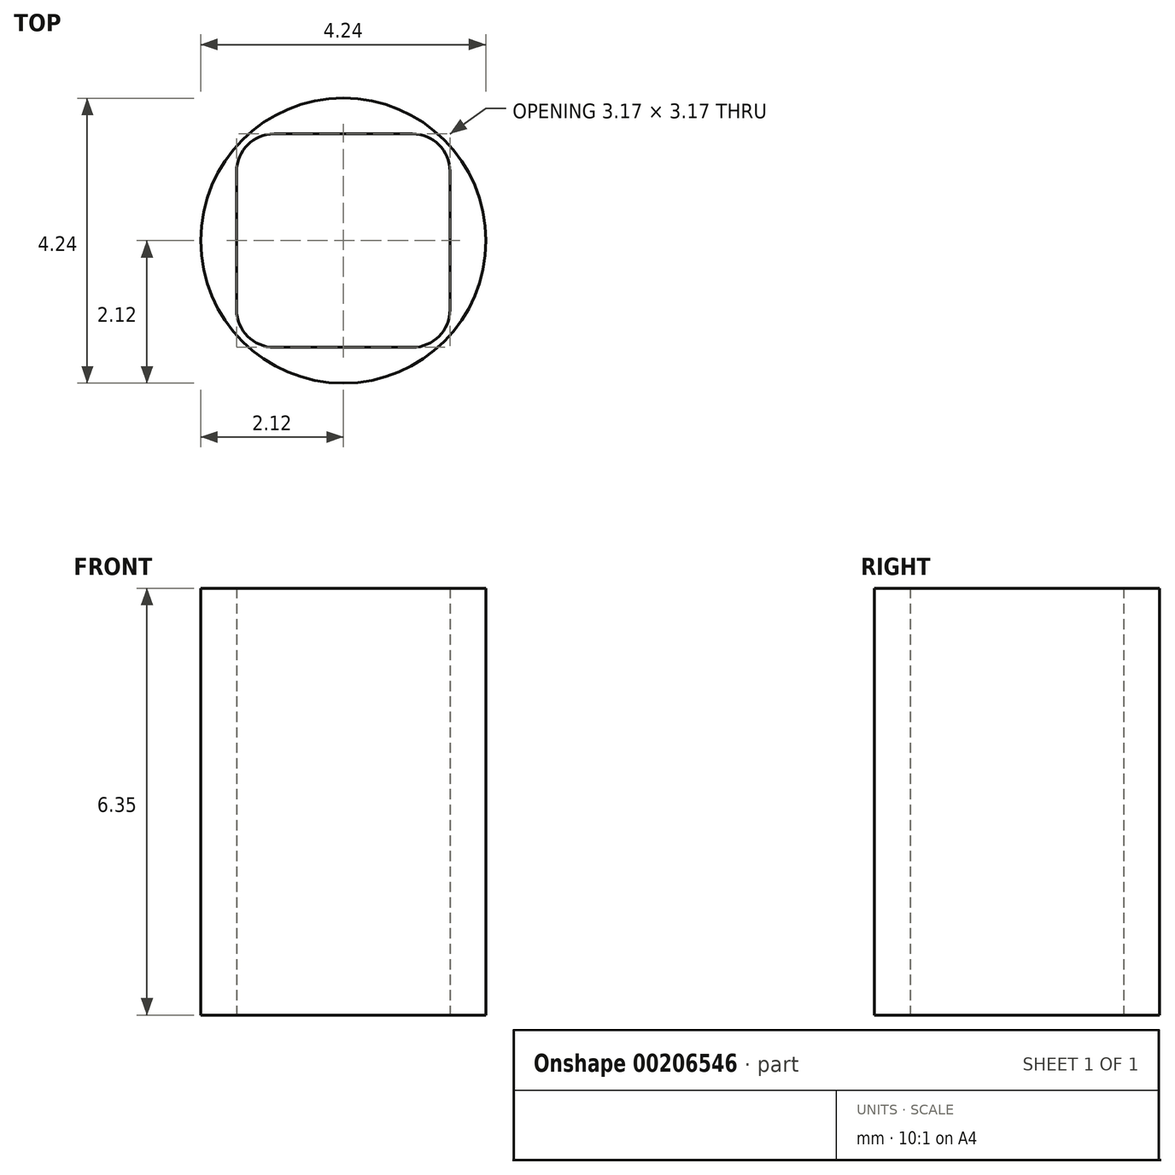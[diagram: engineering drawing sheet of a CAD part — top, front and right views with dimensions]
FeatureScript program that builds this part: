
annotation { "Feature Type Name" : "Feature", "Feature Type Description" : "" }
export const myFeature = defineFeature(function(context is Context, id is Id, definition is map)
    precondition{}
    {
        {
            var Q0;
            Q0=qCreatedBy(makeId("Top.planeOp"),FACE);
            var sketch = newSketch(context, id + "F0", { "sketchPlane" : qUnion([Q0])});
            skCircle(sketch, "E0", {"center": v(0, 0) * mm, "radius": 2.12 * mm});
            skSolve(sketch);
        }
        {
            var Q0;
            Q0=makeQuery(id+"F0.imprint","IMPRINT",FACE,{"disambiguationData":[TD([[makeQuery(id+"F0.imprint","IMPRINT",EDGE,{"derivedFrom":sQuery(id+"F0.wireOp",EDGE,"E0")}),1.0]])]});
            extrude(context, id + "F1", {"entities" : qUnion([Q0]), "depth" : 6.35 * mm});
        }
        {
            var Q0;
            Q0=qCreatedBy(makeId("Top.planeOp"),FACE);
            var sketch = newSketch(context, id + "F2", { "sketchPlane" : qUnion([Q0])});
            skLineSegment(sketch, "E1.bottom", {"start": v(-1.03, 1.59) * mm, "end": v(1.03, 1.59) * mm});
            skLineSegment(sketch, "E1.top", {"start": v(-1.03, -1.59) * mm, "end": v(1.03, -1.59) * mm});
            skLineSegment(sketch, "E1.left", {"start": v(-1.59, 1.03) * mm, "end": v(-1.59, -1.03) * mm});
            skLineSegment(sketch, "E1.right", {"start": v(1.59, 1.03) * mm, "end": v(1.59, -1.03) * mm});
            skPoint(sketch, "E2.visualSharp", {"position": v(-1.59, 1.59) * mm});
            skArc(sketch, "E2.filletArc", {"start": v(-1.03, 1.59) * mm, "mid": v(-1.42, 1.42) * mm, "end": v(-1.59, 1.03) * mm});
            skPoint(sketch, "E3.visualSharp", {"position": v(1.59, 1.59) * mm});
            skArc(sketch, "E3.filletArc", {"start": v(1.59, 1.03) * mm, "mid": v(1.42, 1.42) * mm, "end": v(1.03, 1.59) * mm});
            skPoint(sketch, "E4.visualSharp", {"position": v(1.59, -1.59) * mm});
            skArc(sketch, "E4.filletArc", {"start": v(1.03, -1.59) * mm, "mid": v(1.42, -1.42) * mm, "end": v(1.59, -1.03) * mm});
            skPoint(sketch, "E5.visualSharp", {"position": v(-1.59, -1.59) * mm});
            skArc(sketch, "E5.filletArc", {"start": v(-1.59, -1.03) * mm, "mid": v(-1.42, -1.42) * mm, "end": v(-1.03, -1.59) * mm});
            skSolve(sketch);
        }
        {
            var Q0;
            Q0=makeQuery(id+"F2.imprint","IMPRINT",FACE,{"disambiguationData":[TD([[makeQuery(id+"F2.imprint","IMPRINT",EDGE,{"derivedFrom":sQuery(id+"F2.wireOp",EDGE,"E1.bottom")}),-1.0]])]});
            extrude(context, id + "F3", {"entities" : qUnion([Q0]), "operationType" : NewBodyOperationType.REMOVE, "depth" : 25.4 * mm});
        }
    });
